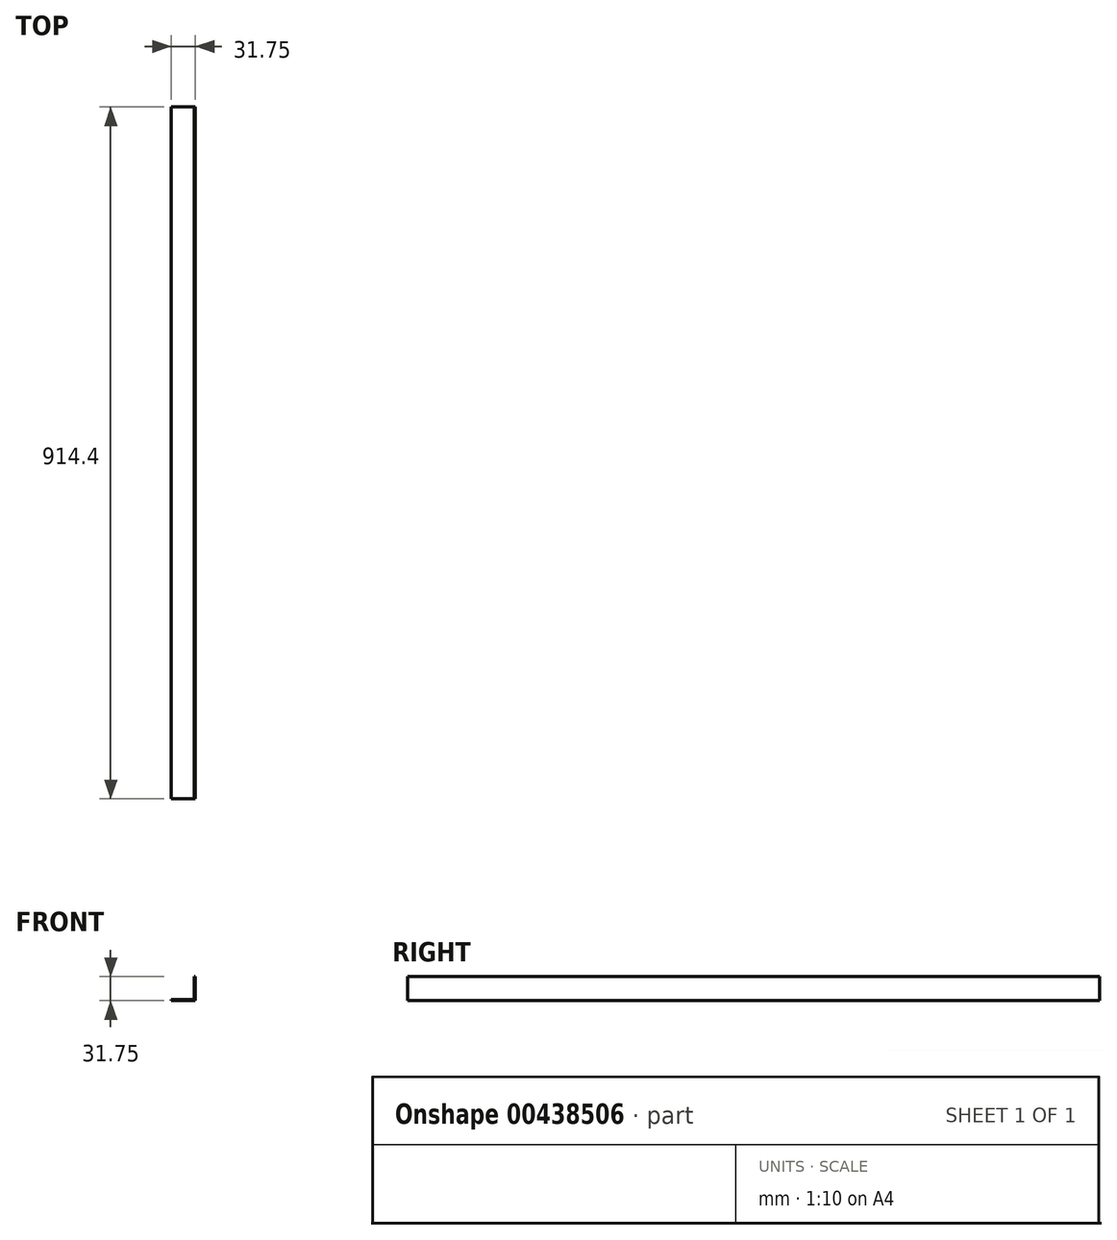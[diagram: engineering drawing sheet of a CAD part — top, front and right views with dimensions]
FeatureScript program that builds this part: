
annotation { "Feature Type Name" : "Feature", "Feature Type Description" : "" }
export const myFeature = defineFeature(function(context is Context, id is Id, definition is map)
    precondition{}
    {
        {
            var Q0;
            Q0=qCreatedBy(makeId("Front.planeOp"),FACE);
            var sketch = newSketch(context, id + "F0", { "sketchPlane" : qUnion([Q0])});
            skLineSegment(sketch, "E0", {"start": v(0, 0) * mm, "end": v(0, 31.75) * mm});
            skLineSegment(sketch, "E1", {"start": v(0, 31.75) * mm, "end": v(-1.2, 31.75) * mm});
            skLineSegment(sketch, "E2", {"start": v(-1.2, 31.75) * mm, "end": v(-1.2, 1.2) * mm});
            skLineSegment(sketch, "E3", {"start": v(-1.2, 1.2) * mm, "end": v(-31.75, 1.2) * mm});
            skLineSegment(sketch, "E4", {"start": v(-31.75, 1.2) * mm, "end": v(-31.75, 0) * mm});
            skLineSegment(sketch, "E5", {"start": v(-31.75, 0) * mm, "end": v(0, 0) * mm});
            skSolve(sketch);
        }
        {
            var Q0;
            Q0 = qSketchRegion(id + "F0", true);
            extrude(context, id + "F1", {"entities" : qUnion([Q0]), "depth" : 914.4 * mm});
        }
    });
